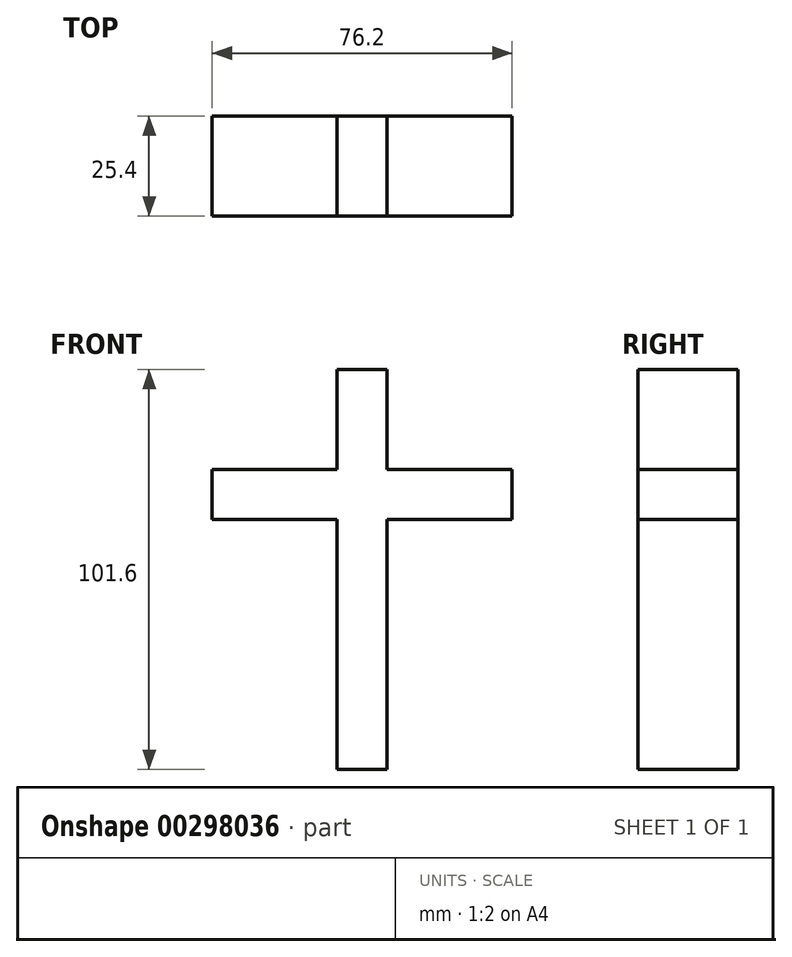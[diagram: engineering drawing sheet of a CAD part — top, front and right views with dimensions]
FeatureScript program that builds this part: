
annotation { "Feature Type Name" : "Feature", "Feature Type Description" : "" }
export const myFeature = defineFeature(function(context is Context, id is Id, definition is map)
    precondition{}
    {
        {
            var Q0;
            Q0=qCreatedBy(makeId("Front.planeOp"),FACE);
            var sketch = newSketch(context, id + "F0", { "sketchPlane" : qUnion([Q0])});
            skLineSegment(sketch, "E0", {"start": v(0, 0) * mm, "end": v(0, 63.5) * mm});
            skLineSegment(sketch, "E1", {"start": v(0, 63.5) * mm, "end": v(31.75, 63.5) * mm});
            skLineSegment(sketch, "E2", {"start": v(31.75, 63.5) * mm, "end": v(31.75, 76.2) * mm});
            skLineSegment(sketch, "E3", {"start": v(31.75, 76.2) * mm, "end": v(0, 76.2) * mm});
            skPoint(sketch, "E3.endSnap0", {"position": v(0, 31.75) * mm});
            skLineSegment(sketch, "E4", {"start": v(0, 76.2) * mm, "end": v(0, 101.6) * mm});
            skLineSegment(sketch, "E5", {"start": v(0, 101.6) * mm, "end": v(-12.7, 101.6) * mm});
            skLineSegment(sketch, "E6", {"start": v(-12.7, 101.6) * mm, "end": v(-12.7, 76.2) * mm});
            skLineSegment(sketch, "E7", {"start": v(-12.7, 76.2) * mm, "end": v(-44.45, 76.2) * mm});
            skLineSegment(sketch, "E8", {"start": v(-44.45, 76.2) * mm, "end": v(-44.45, 63.5) * mm});
            skLineSegment(sketch, "E9", {"start": v(-44.45, 63.5) * mm, "end": v(-12.7, 63.5) * mm});
            skLineSegment(sketch, "E10", {"start": v(-12.7, 63.5) * mm, "end": v(-12.7, 0) * mm});
            skLineSegment(sketch, "E11", {"start": v(-12.7, 0) * mm, "end": v(0, 0) * mm});
            skSolve(sketch);
        }
        {
            var Q0;
            Q0 = qSketchRegion(id + "F0", true);
            extrude(context, id + "F1", {"entities" : qUnion([Q0]), "depth" : 25.4 * mm});
        }
    });
